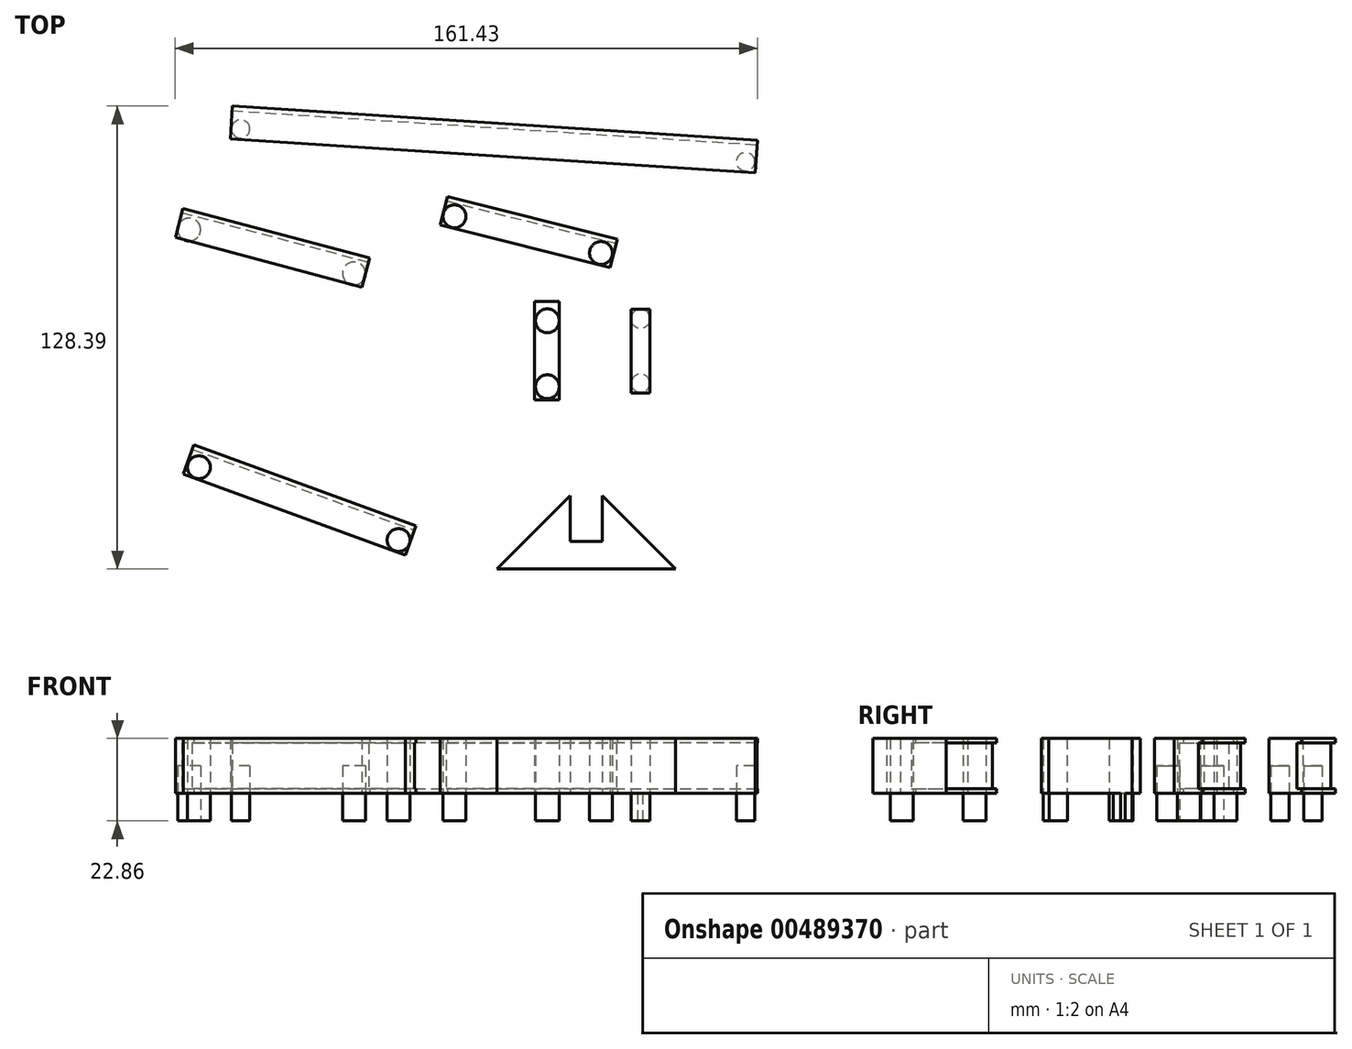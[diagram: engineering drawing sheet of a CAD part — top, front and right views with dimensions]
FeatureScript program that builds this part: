
annotation { "Feature Type Name" : "Feature", "Feature Type Description" : "" }
export const myFeature = defineFeature(function(context is Context, id is Id, definition is map)
    precondition{}
    {
        {
            var Q0;
            Q0=qCreatedBy(makeId("Top.planeOp"),FACE);
            var sketch = newSketch(context, id + "F0", { "sketchPlane" : qUnion([Q0])});
            skCircle(sketch, "E0", {"center": v(-70.13, 38.27) * mm, "radius": 3.18 * mm});
            skCircle(sketch, "E1", {"center": v(-24.4, 26.1) * mm, "radius": 3.18 * mm});
            skLineSegment(sketch, "E2", {"start": v(-70.13, 38.27) * mm, "end": v(-24.4, 26.1) * mm});
            skSolve(sketch);
        }
        {
            var Q0;
            Q0=qCreatedBy(makeId("Top.planeOp"),FACE);
            var sketch = newSketch(context, id + "F1", { "sketchPlane" : qUnion([Q0])});
            skCircle(sketch, "E3", {"center": v(-67.41, -27.65) * mm, "radius": 3.18 * mm});
            skCircle(sketch, "E4", {"center": v(-12.03, -47.84) * mm, "radius": 3.18 * mm});
            skLineSegment(sketch, "E5", {"start": v(-67.41, -27.65) * mm, "end": v(-12.03, -47.84) * mm});
            skSolve(sketch);
        }
        {
            var Q0;
            Q0 = qSketchRegion(id + "F1", true);
            extrude(context, id + "F2", {"entities" : qUnion([Q0]), "oppositeDirection" : true, "depth" : 7.62 * mm});
        }
        {
            var Q0;
            Q0=makeQuery(id+"F2.opExtrude","CAP_FACE",FACE,{"disambiguationData":[OSD([sQuery(id+"F1.wireOp",EDGE,"E3")])],"isStart":true});
            var Q1;
            Q1=makeQuery(id+"F2.opExtrude","CAP_FACE",FACE,{"disambiguationData":[OSD([sQuery(id+"F1.wireOp",EDGE,"E4")])],"isStart":true});
            extrude(context, id + "F3", {"entities" : qUnion([Q0, Q1]), "depth" : 15.24 * mm});
        }
        {
            var Q0;
            Q0=qCreatedBy(makeId("Top.planeOp"),FACE);
            var sketch = newSketch(context, id + "F4", { "sketchPlane" : qUnion([Q0])});
            skLineSegment(sketch, "E6", {"start": v(-71.78, -29.52) * mm, "end": v(-68.85, -21.47) * mm});
            skLineSegment(sketch, "E7", {"start": v(-68.85, -21.47) * mm, "end": v(-7.18, -43.95) * mm});
            skLineSegment(sketch, "E8", {"start": v(-7.18, -43.95) * mm, "end": v(-10.12, -52) * mm});
            skLineSegment(sketch, "E9", {"start": v(-10.12, -52) * mm, "end": v(-71.78, -29.52) * mm});
            skSolve(sketch);
        }
        {
            var Q0;
            Q0=makeQuery(id+"F4.imprint","IMPRINT",FACE,{"disambiguationData":[TD([[makeQuery(id+"F4.imprint","IMPRINT",EDGE,{"derivedFrom":sQuery(id+"F4.wireOp",EDGE,"E6")}),-1.0]])]});
            extrude(context, id + "F5", {"entities" : qUnion([Q0]), "depth" : 15.24 * mm});
        }
        {
            var Q0;
            Q0=makeQuery(id+"F5.opExtrude","SWEPT_FACE",FACE,{"disambiguationData":[OSD([sQuery(id+"F4.wireOp",EDGE,"E7")])]});
            var sketch = newSketch(context, id + "F6", { "sketchPlane" : qUnion([Q0])});
            skLineSegment(sketch, "E10.0", {"start": v(57.33, 15.24) * mm, "end": v(-8.3, 15.24) * mm});
            skLineSegment(sketch, "E10.1", {"start": v(57.33, 0) * mm, "end": v(-8.3, 0) * mm});
            skLineSegment(sketch, "E11", {"start": v(57.33, 13.97) * mm, "end": v(-8.3, 13.97) * mm});
            skLineSegment(sketch, "E12", {"start": v(-8.3, 1.27) * mm, "end": v(57.33, 1.27) * mm});
            skLineSegment(sketch, "E13", {"start": v(-8.3, 13.97) * mm, "end": v(-8.3, 1.27) * mm});
            skLineSegment(sketch, "E14", {"start": v(57.33, 13.97) * mm, "end": v(57.33, 1.27) * mm});
            skSolve(sketch);
        }
        {
            var Q0;
            Q0=makeQuery(id+"F6.imprint","IMPRINT",FACE,{"disambiguationData":[TD([[makeQuery(id+"F6.imprint","IMPRINT",EDGE,{"derivedFrom":sQuery(id+"F6.wireOp",EDGE,"E11")}),1.0]])]});
            extrude(context, id + "F7", {"entities" : qUnion([Q0]), "operationType" : NewBodyOperationType.REMOVE, "oppositeDirection" : true, "depth" : 0.76 * mm});
        }
        {
            var Q0;
            Q0=qCreatedBy(makeId("Top.planeOp"),FACE);
            var sketch = newSketch(context, id + "F8", { "sketchPlane" : qUnion([Q0])});
            skCircle(sketch, "E15", {"center": v(3.47, 41.93) * mm, "radius": 3.18 * mm});
            skCircle(sketch, "E16", {"center": v(44.1, 31.77) * mm, "radius": 3.18 * mm});
            skLineSegment(sketch, "E17", {"start": v(3.47, 41.93) * mm, "end": v(44.1, 31.77) * mm});
            skSolve(sketch);
        }
        {
            var Q0;
            Q0=makeQuery(id+"F8.imprint","IMPRINT",FACE,{"disambiguationData":[TD([[makeQuery(id+"F8.imprint","IMPRINT",EDGE,{"derivedFrom":sQuery(id+"F8.wireOp",EDGE,"E15")}),1.0]])]});
            var Q1;
            Q1=makeQuery(id+"F8.imprint","IMPRINT",FACE,{"disambiguationData":[TD([[makeQuery(id+"F8.imprint","IMPRINT",EDGE,{"derivedFrom":sQuery(id+"F8.wireOp",EDGE,"E16")}),1.0]])]});
            extrude(context, id + "F9", {"entities" : qUnion([Q0, Q1]), "oppositeDirection" : true, "depth" : 7.62 * mm});
        }
        {
            var Q0;
            Q0=makeQuery(id+"F9.opExtrude","CAP_FACE",FACE,{"disambiguationData":[OSD([sQuery(id+"F8.wireOp",EDGE,"E15")])],"isStart":true});
            var Q1;
            Q1=makeQuery(id+"F9.opExtrude","CAP_FACE",FACE,{"disambiguationData":[OSD([sQuery(id+"F8.wireOp",EDGE,"E16")])],"isStart":true});
            extrude(context, id + "F10", {"entities" : qUnion([Q0, Q1]), "depth" : 15.24 * mm});
        }
        {
            var Q0;
            Q0=qCreatedBy(makeId("Top.planeOp"),FACE);
            var sketch = newSketch(context, id + "F11", { "sketchPlane" : qUnion([Q0])});
            skLineSegment(sketch, "E18", {"start": v(1.5, 47.44) * mm, "end": v(48.63, 35.66) * mm});
            skLineSegment(sketch, "E19", {"start": v(46.67, 27.79) * mm, "end": v(-0.47, 39.57) * mm});
            skLineSegment(sketch, "E20", {"start": v(48.63, 35.66) * mm, "end": v(46.67, 27.79) * mm});
            skLineSegment(sketch, "E21", {"start": v(1.5, 47.44) * mm, "end": v(-0.47, 39.57) * mm});
            skSolve(sketch);
        }
        {
            var Q0;
            Q0=makeQuery(id+"F11.imprint","IMPRINT",FACE,{"disambiguationData":[TD([[makeQuery(id+"F11.imprint","IMPRINT",EDGE,{"derivedFrom":sQuery(id+"F11.wireOp",EDGE,"E18")}),-1.0]])]});
            extrude(context, id + "F12", {"entities" : qUnion([Q0]), "depth" : 15.24 * mm});
        }
        {
            var Q0;
            Q0=makeQuery(id+"F12.opExtrude","SWEPT_FACE",FACE,{"disambiguationData":[OSD([sQuery(id+"F11.wireOp",EDGE,"E18")])]});
            var sketch = newSketch(context, id + "F13", { "sketchPlane" : qUnion([Q0])});
            skLineSegment(sketch, "E22.0", {"start": v(10.05, 0) * mm, "end": v(-38.53, 0) * mm});
            skLineSegment(sketch, "E22.1", {"start": v(10.05, 15.24) * mm, "end": v(-38.53, 15.24) * mm});
            skLineSegment(sketch, "E23", {"start": v(10.05, 13.97) * mm, "end": v(-38.53, 13.97) * mm});
            skLineSegment(sketch, "E24", {"start": v(-38.53, 1.27) * mm, "end": v(10.05, 1.27) * mm});
            skLineSegment(sketch, "E25", {"start": v(10.05, 1.27) * mm, "end": v(10.05, 13.97) * mm});
            skLineSegment(sketch, "E26", {"start": v(-38.53, 1.27) * mm, "end": v(-38.53, 13.97) * mm});
            skSolve(sketch);
        }
        {
            var Q0;
            Q0=makeQuery(id+"F13.imprint","IMPRINT",FACE,{"disambiguationData":[TD([[makeQuery(id+"F13.imprint","IMPRINT",EDGE,{"derivedFrom":sQuery(id+"F13.wireOp",EDGE,"E23")}),1.0]])]});
            extrude(context, id + "F14", {"entities" : qUnion([Q0]), "operationType" : NewBodyOperationType.REMOVE, "oppositeDirection" : true, "depth" : 1.27 * mm, "offsetDistance" : 25.4 * mm});
        }
        {
            var Q0;
            Q0=qCreatedBy(makeId("Top.planeOp"),FACE);
            var sketch = newSketch(context, id + "F15", { "sketchPlane" : qUnion([Q0])});
            skCircle(sketch, "E27", {"center": v(29.22, 12.98) * mm, "radius": 3.3 * mm});
            skCircle(sketch, "E28", {"center": v(29.22, -5.3) * mm, "radius": 3.3 * mm});
            skSolve(sketch);
        }
        {
            var Q0;
            Q0=makeQuery(id+"F15.imprint","IMPRINT",FACE,{"disambiguationData":[TD([[makeQuery(id+"F15.imprint","IMPRINT",EDGE,{"derivedFrom":sQuery(id+"F15.wireOp",EDGE,"E27")}),1.0]])]});
            var Q1;
            Q1=makeQuery(id+"F15.imprint","IMPRINT",FACE,{"disambiguationData":[TD([[makeQuery(id+"F15.imprint","IMPRINT",EDGE,{"derivedFrom":sQuery(id+"F15.wireOp",EDGE,"E28")}),1.0]])]});
            extrude(context, id + "F16", {"entities" : qUnion([Q0, Q1]), "oppositeDirection" : true, "depth" : 7.62 * mm});
        }
        {
            var Q0;
            Q0=makeQuery(id+"F16.opExtrude","CAP_FACE",FACE,{"disambiguationData":[OSD([sQuery(id+"F15.wireOp",EDGE,"E27")])],"isStart":true});
            var Q1;
            Q1=makeQuery(id+"F16.opExtrude","CAP_FACE",FACE,{"disambiguationData":[OSD([sQuery(id+"F15.wireOp",EDGE,"E28")])],"isStart":true});
            extrude(context, id + "F17", {"entities" : qUnion([Q0, Q1]), "depth" : 15.24 * mm});
        }
        {
            var Q0;
            Q0=qCreatedBy(makeId("Top.planeOp"),FACE);
            var sketch = newSketch(context, id + "F18", { "sketchPlane" : qUnion([Q0])});
            skLineSegment(sketch, "E29.bottom", {"start": v(25.72, 18.35) * mm, "end": v(32.46, 18.35) * mm});
            skLineSegment(sketch, "E29.top", {"start": v(25.72, -9.03) * mm, "end": v(32.46, -9.03) * mm});
            skLineSegment(sketch, "E29.left", {"start": v(25.72, 18.35) * mm, "end": v(25.72, -9.03) * mm});
            skLineSegment(sketch, "E29.right", {"start": v(32.46, 18.35) * mm, "end": v(32.46, -9.03) * mm});
            skSolve(sketch);
        }
        {
            var Q0;
            Q0=makeQuery(id+"F18.imprint","IMPRINT",FACE,{"disambiguationData":[TD([[makeQuery(id+"F18.imprint","IMPRINT",EDGE,{"derivedFrom":sQuery(id+"F18.wireOp",EDGE,"E29.bottom")}),-1.0]])]});
            extrude(context, id + "F19", {"entities" : qUnion([Q0]), "depth" : 15.24 * mm});
        }
        {
            var Q0;
            Q0=qCreatedBy(makeId("Top.planeOp"),FACE);
            var sketch = newSketch(context, id + "F20", { "sketchPlane" : qUnion([Q0])});
            skLineSegment(sketch, "E30", {"start": v(35.53, -35.56) * mm, "end": v(15.2, -55.88) * mm});
            skLineSegment(sketch, "E31", {"start": v(15.2, -55.88) * mm, "end": v(64.74, -55.88) * mm});
            skLineSegment(sketch, "E32", {"start": v(64.74, -55.88) * mm, "end": v(44.42, -35.56) * mm});
            skLineSegment(sketch, "E33", {"start": v(44.42, -35.56) * mm, "end": v(44.42, -48.26) * mm});
            skLineSegment(sketch, "E34", {"start": v(44.42, -48.26) * mm, "end": v(35.53, -48.26) * mm});
            skLineSegment(sketch, "E35", {"start": v(35.53, -48.26) * mm, "end": v(35.53, -35.56) * mm});
            skSolve(sketch);
        }
        {
            var Q0;
            Q0=makeQuery(id+"F20.imprint","IMPRINT",FACE,{"disambiguationData":[TD([[makeQuery(id+"F20.imprint","IMPRINT",EDGE,{"derivedFrom":sQuery(id+"F20.wireOp",EDGE,"E30")}),1.0]])]});
            extrude(context, id + "F21", {"entities" : qUnion([Q0]), "depth" : 15.24 * mm});
        }
        {
            var Q0;
            Q0=makeQuery(id+"F0.imprint","IMPRINT",FACE,{"disambiguationData":[TD([[makeQuery(id+"F0.imprint","IMPRINT",EDGE,{"derivedFrom":sQuery(id+"F0.wireOp",EDGE,"E0")}),1.0]])]});
            var Q1;
            Q1=makeQuery(id+"F0.imprint","IMPRINT",FACE,{"disambiguationData":[TD([[makeQuery(id+"F0.imprint","IMPRINT",EDGE,{"derivedFrom":sQuery(id+"F0.wireOp",EDGE,"E1")}),1.0]])]});
            extrude(context, id + "F22", {"entities" : qUnion([Q0, Q1]), "endBound" : BoundingType.SYMMETRIC, "depth" : 15.24 * mm, "offsetDistance" : 25.4 * mm});
        }
        {
            var Q0;
            Q0=qCreatedBy(makeId("Top.planeOp"),FACE);
            var sketch = newSketch(context, id + "F23", { "sketchPlane" : qUnion([Q0])});
            skLineSegment(sketch, "E36", {"start": v(-73.98, 36.05) * mm, "end": v(-22.16, 22.27) * mm});
            skLineSegment(sketch, "E37", {"start": v(-22.16, 22.27) * mm, "end": v(-20.01, 30.34) * mm});
            skLineSegment(sketch, "E38", {"start": v(-20.01, 30.34) * mm, "end": v(-71.83, 44.12) * mm});
            skLineSegment(sketch, "E39", {"start": v(-73.98, 36.05) * mm, "end": v(-71.83, 44.12) * mm});
            skSolve(sketch);
        }
        {
            var Q0;
            Q0=makeQuery(id+"F23.imprint","IMPRINT",FACE,{"disambiguationData":[TD([[makeQuery(id+"F23.imprint","IMPRINT",EDGE,{"derivedFrom":sQuery(id+"F23.wireOp",EDGE,"E36")}),1.0]])]});
            extrude(context, id + "F24", {"entities" : qUnion([Q0]), "depth" : 15.24 * mm});
        }
        {
            var Q0;
            Q0=makeQuery(id+"F24.opExtrude","SWEPT_FACE",FACE,{"disambiguationData":[OSD([sQuery(id+"F23.wireOp",EDGE,"E38")])]});
            var sketch = newSketch(context, id + "F25", { "sketchPlane" : qUnion([Q0])});
            skLineSegment(sketch, "E40.0", {"start": v(27.14, 15.24) * mm, "end": v(80.76, 15.24) * mm});
            skLineSegment(sketch, "E40.1", {"start": v(27.14, 15.24) * mm, "end": v(27.14, 0) * mm});
            skLineSegment(sketch, "E40.2", {"start": v(27.14, 0) * mm, "end": v(80.76, 0) * mm});
            skLineSegment(sketch, "E40.3", {"start": v(80.76, 15.24) * mm, "end": v(80.76, 0) * mm});
            skLineSegment(sketch, "E41", {"start": v(27.14, 13.97) * mm, "end": v(80.76, 13.97) * mm});
            skLineSegment(sketch, "E42", {"start": v(80.76, 1.27) * mm, "end": v(27.14, 1.27) * mm});
            skLineSegment(sketch, "E43", {"start": v(27.14, 13.97) * mm, "end": v(27.14, 1.27) * mm});
            skLineSegment(sketch, "E44", {"start": v(80.76, 1.27) * mm, "end": v(80.76, 13.97) * mm});
            skSolve(sketch);
        }
        {
            var Q0;
            Q0=makeQuery(id+"F25.imprint","IMPRINT",FACE,{"disambiguationData":[TD([[makeQuery(id+"F25.imprint","IMPRINT",EDGE,{"derivedFrom":sQuery(id+"F25.wireOp",EDGE,"E41")}),-1.0]])]});
            extrude(context, id + "F26", {"entities" : qUnion([Q0]), "operationType" : NewBodyOperationType.REMOVE, "oppositeDirection" : true, "depth" : 1.27 * mm});
        }
        {
            var Q0;
            Q0=makeQuery(id+"F5.opExtrude","SWEPT_BODY",BODY,{"disambiguationData":[OSD([sQuery(id+"F4.wireOp",EDGE,"E6"),sQuery(id+"F4.wireOp",EDGE,"E7"),sQuery(id+"F4.wireOp",EDGE,"E8"),sQuery(id+"F4.wireOp",EDGE,"E9")])]});
            deleteBodies(context, id + "F27", {"entities" : qUnion([Q0])});
        }
        {
            var Q0;
            Q0=makeQuery(id+"F4.imprint","IMPRINT",FACE,{"disambiguationData":[TD([[makeQuery(id+"F4.imprint","IMPRINT",EDGE,{"derivedFrom":sQuery(id+"F4.wireOp",EDGE,"E6")}),-1.0]])]});
            extrude(context, id + "F28", {"entities" : qUnion([Q0]), "depth" : 15.24 * mm});
        }
        {
            var Q0;
            Q0=makeQuery(id+"F28.opExtrude","SWEPT_FACE",FACE,{"disambiguationData":[OSD([sQuery(id+"F4.wireOp",EDGE,"E7")])]});
            var sketch = newSketch(context, id + "F29", { "sketchPlane" : qUnion([Q0])});
            skLineSegment(sketch, "E45.0", {"start": v(57.33, 15.24) * mm, "end": v(-8.3, 15.24) * mm});
            skLineSegment(sketch, "E45.1", {"start": v(57.33, 15.24) * mm, "end": v(57.33, 0) * mm});
            skLineSegment(sketch, "E45.2", {"start": v(57.33, 0) * mm, "end": v(-8.3, 0) * mm});
            skLineSegment(sketch, "E45.3", {"start": v(-8.3, 15.24) * mm, "end": v(-8.3, 0) * mm});
            skLineSegment(sketch, "E46", {"start": v(57.33, 13.97) * mm, "end": v(-8.3, 13.97) * mm});
            skLineSegment(sketch, "E47", {"start": v(-8.3, 13.97) * mm, "end": v(-8.3, 1.27) * mm});
            skLineSegment(sketch, "E48", {"start": v(-8.3, 1.27) * mm, "end": v(57.33, 1.27) * mm});
            skLineSegment(sketch, "E49", {"start": v(57.33, 1.27) * mm, "end": v(57.33, 13.97) * mm});
            skSolve(sketch);
        }
        {
            var Q0;
            Q0=makeQuery(id+"F29.imprint","IMPRINT",FACE,{"disambiguationData":[TD([[makeQuery(id+"F29.imprint","IMPRINT",EDGE,{"derivedFrom":sQuery(id+"F29.wireOp",EDGE,"E46")}),1.0]])]});
            extrude(context, id + "F30", {"entities" : qUnion([Q0]), "operationType" : NewBodyOperationType.REMOVE, "oppositeDirection" : true, "depth" : 1.27 * mm});
        }
        {
            var Q0;
            Q0=qCreatedBy(makeId("Top.planeOp"),FACE);
            var sketch = newSketch(context, id + "F31", { "sketchPlane" : qUnion([Q0])});
            skCircle(sketch, "E50", {"center": v(-55.84, 66.18) * mm, "radius": 2.54 * mm});
            skCircle(sketch, "E51", {"center": v(84.2, 57.09) * mm, "radius": 2.54 * mm});
            skLineSegment(sketch, "E52", {"start": v(-55.84, 66.18) * mm, "end": v(84.2, 57.09) * mm, "construction": true});
            skLineSegment(sketch, "E53", {"start": v(-58.11, 72.5) * mm, "end": v(87.45, 63.06) * mm});
            skLineSegment(sketch, "E54", {"start": v(87.45, 63.06) * mm, "end": v(86.86, 54) * mm});
            skLineSegment(sketch, "E55", {"start": v(86.86, 54) * mm, "end": v(-58.7, 63.45) * mm});
            skLineSegment(sketch, "E56", {"start": v(-58.7, 63.45) * mm, "end": v(-58.11, 72.5) * mm});
            skSolve(sketch);
        }
        {
            var Q0;
            Q0=makeQuery(id+"F31.imprint","IMPRINT",FACE,{"disambiguationData":[TD([[makeQuery(id+"F31.imprint","IMPRINT",EDGE,{"derivedFrom":sQuery(id+"F31.wireOp",EDGE,"E50")}),1.0]])]});
            var Q1;
            Q1=makeQuery(id+"F31.imprint","IMPRINT",FACE,{"disambiguationData":[TD([[makeQuery(id+"F31.imprint","IMPRINT",EDGE,{"derivedFrom":sQuery(id+"F31.wireOp",EDGE,"E51")}),1.0]])]});
            extrude(context, id + "F32", {"entities" : qUnion([Q0, Q1]), "endBound" : BoundingType.SYMMETRIC, "depth" : 15.24 * mm, "offsetDistance" : 25.4 * mm});
        }
        {
            var Q0;
            Q0=makeQuery(id+"F31.imprint","IMPRINT",FACE,{"disambiguationData":[TD([[makeQuery(id+"F31.imprint","IMPRINT",EDGE,{"derivedFrom":sQuery(id+"F31.wireOp",EDGE,"E50")}),-1.0]])]});
            var Q1;
            Q1=makeQuery(id+"F31.imprint","IMPRINT",FACE,{"disambiguationData":[TD([[makeQuery(id+"F31.imprint","IMPRINT",EDGE,{"derivedFrom":sQuery(id+"F31.wireOp",EDGE,"E50")}),1.0]])]});
            var Q2;
            Q2=makeQuery(id+"F31.imprint","IMPRINT",FACE,{"disambiguationData":[TD([[makeQuery(id+"F31.imprint","IMPRINT",EDGE,{"derivedFrom":sQuery(id+"F31.wireOp",EDGE,"E51")}),1.0]])]});
            extrude(context, id + "F33", {"entities" : qUnion([Q0, Q1, Q2]), "depth" : 15.24 * mm, "offsetDistance" : 25.4 * mm});
        }
        {
            var Q0;
            Q0=makeQuery(id+"F33.opExtrude","SWEPT_FACE",FACE,{"disambiguationData":[OSD([sQuery(id+"F31.wireOp",EDGE,"E53")])]});
            var sketch = newSketch(context, id + "F34", { "sketchPlane" : qUnion([Q0])});
            skLineSegment(sketch, "E57.0", {"start": v(62.69, 0) * mm, "end": v(-83.18, 0) * mm});
            skLineSegment(sketch, "E57.1", {"start": v(62.69, 15.24) * mm, "end": v(62.69, 0) * mm});
            skLineSegment(sketch, "E57.2", {"start": v(62.69, 15.24) * mm, "end": v(-83.18, 15.24) * mm});
            skLineSegment(sketch, "E57.3", {"start": v(-83.18, 15.24) * mm, "end": v(-83.18, 0) * mm});
            skLineSegment(sketch, "E58", {"start": v(62.69, 1.27) * mm, "end": v(-83.18, 1.27) * mm});
            skLineSegment(sketch, "E59", {"start": v(-83.18, 13.97) * mm, "end": v(62.69, 13.97) * mm});
            skSolve(sketch);
        }
        {
            var Q0;
            {var subQ0=sQuery(id+"F34.wireOp",EDGE,"E58");Q0=makeQuery(id+"F34.imprint","IMPRINT",FACE,{"disambiguationData":[TD([[makeQuery(id+"F34.imprint","IMPRINT",EDGE,{"derivedFrom":subQ0}),-1.0]])]});}
            extrude(context, id + "F35", {"entities" : qUnion([Q0]), "operationType" : NewBodyOperationType.REMOVE, "oppositeDirection" : true, "depth" : 1.27 * mm, "offsetDistance" : 25.4 * mm});
        }
        {
            var Q0;
            Q0=qCreatedBy(makeId("Top.planeOp"),FACE);
            var sketch = newSketch(context, id + "F36", { "sketchPlane" : qUnion([Q0])});
            skCircle(sketch, "E60", {"center": v(55.06, 13.56) * mm, "radius": 2.67 * mm});
            skCircle(sketch, "E61", {"center": v(55.06, -4.36) * mm, "radius": 2.55 * mm});
            skLineSegment(sketch, "E62.bottom", {"start": v(52.43, 16.11) * mm, "end": v(57.64, 16.11) * mm});
            skLineSegment(sketch, "E62.top", {"start": v(52.43, -7) * mm, "end": v(57.64, -7) * mm});
            skLineSegment(sketch, "E62.left", {"start": v(52.43, 16.11) * mm, "end": v(52.43, -7) * mm});
            skLineSegment(sketch, "E62.right", {"start": v(57.64, 16.11) * mm, "end": v(57.64, -7) * mm});
            skSolve(sketch);
        }
        {
            var Q0;
            Q0=makeQuery(id+"F36.imprint","IMPRINT",FACE,{"disambiguationData":[TD([[makeQuery(id+"F36.imprint","IMPRINT",EDGE,{"derivedFrom":sQuery(id+"F36.wireOp",EDGE,"E60")}),-1.0]])]});
            var Q1;
            Q1=makeQuery(id+"F36.imprint","IMPRINT",FACE,{"disambiguationData":[TD([[makeQuery(id+"F36.imprint","IMPRINT",EDGE,{"derivedFrom":sQuery(id+"F36.wireOp",EDGE,"E60")}),1.0]])]});
            var Q2;
            Q2=makeQuery(id+"F36.imprint","IMPRINT",FACE,{"disambiguationData":[TD([[makeQuery(id+"F36.imprint","IMPRINT",EDGE,{"derivedFrom":sQuery(id+"F36.wireOp",EDGE,"E61")}),1.0]])]});
            var Q3;
            Q3=makeQuery(id+"F36.imprint","IMPRINT",FACE,{"disambiguationData":[TD([[makeQuery(id+"F36.imprint","IMPRINT",EDGE,{"derivedFrom":sQuery(id+"F36.wireOp",EDGE,"E61")}),-1.0]])]});
            extrude(context, id + "F37", {"entities" : qUnion([Q0, Q1, Q2, Q3]), "depth" : 15.24 * mm, "offsetDistance" : 25.4 * mm});
        }
        {
            var Q0;
            Q0=makeQuery(id+"F36.imprint","IMPRINT",FACE,{"disambiguationData":[TD([[makeQuery(id+"F36.imprint","IMPRINT",EDGE,{"derivedFrom":sQuery(id+"F36.wireOp",EDGE,"E60")}),1.0]])]});
            var Q1;
            Q1=makeQuery(id+"F36.imprint","IMPRINT",FACE,{"disambiguationData":[TD([[makeQuery(id+"F36.imprint","IMPRINT",EDGE,{"derivedFrom":sQuery(id+"F36.wireOp",EDGE,"E61")}),1.0]])]});
            extrude(context, id + "F38", {"entities" : qUnion([Q0, Q1]), "operationType" : NewBodyOperationType.ADD, "oppositeDirection" : true, "depth" : 7.62 * mm, "offsetDistance" : 25.4 * mm});
        }
    });
